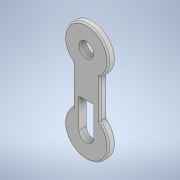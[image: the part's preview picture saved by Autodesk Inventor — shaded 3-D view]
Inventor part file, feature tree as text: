
AUTODESK INVENTOR PART (.ipt)
format: ipt  version: 2022 (Build 260153000, 153)  size: 163,840 bytes
history: native  units: in
note: dims shown in document units (in); Inventor stores cm internally (conversion verified against a paired STEP export)
features: extrude x2, sketch x2, fillet x1
ambient origin geometry x8: Origin, YZ Plane, XZ Plane, XY Plane, X Axis, Y Axis, Z Axis, Center Point
bodies: Solid1 (feature_tree)
feature tree (5):
  extrude  "Extrusion1"  Depth=0.7874in
  fillet  "Fillet1"  Radius=2.3622in
  extrude  "Extrusion2"  Depth=0.7874in
  sketch  "Sketch1"  dims[d2=0.7874in d3=1.5945in d4=2.3622in]
  sketch  "Sketch2"  dims[d5=0.7874in d6=1.4173in d7=3.937in d8=2.3622in d9=0.7874in d10=0.3937in d11=0.0in d12=0.0787in d13=0.7874in d14=1.5945in d15=0.4188in d16=0.0in]
